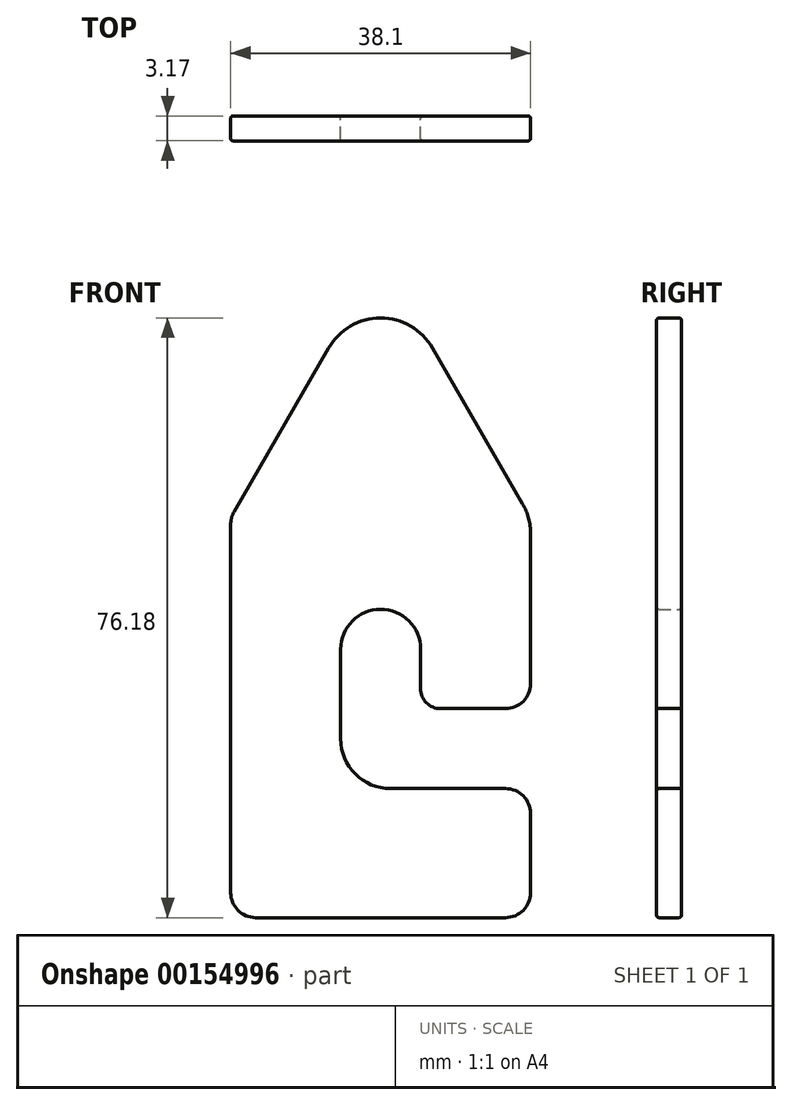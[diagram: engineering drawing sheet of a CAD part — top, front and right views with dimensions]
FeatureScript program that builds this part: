
annotation { "Feature Type Name" : "Feature", "Feature Type Description" : "" }
export const myFeature = defineFeature(function(context is Context, id is Id, definition is map)
    precondition{}
    {
        {
            var Q0;
            Q0=qCreatedBy(makeId("Front.planeOp"),FACE);
            var sketch = newSketch(context, id + "F0", { "sketchPlane" : qUnion([Q0])});
            skLineSegment(sketch, "E0.top", {"start": v(-15.88, -24.24) * mm, "end": v(15.87, -24.24) * mm});
            skLineSegment(sketch, "E0.left", {"start": v(-19.05, 25.7) * mm, "end": v(-19.05, -21.07) * mm});
            skLineSegment(sketch, "E0.right", {"start": v(19.05, 24.52) * mm, "end": v(19.05, 5.48) * mm});
            skLineSegment(sketch, "E1", {"start": v(19.05, -11.03) * mm, "end": v(19.05, -21.07) * mm});
            skLineSegment(sketch, "E2.bottom", {"start": v(15.88, -7.85) * mm, "end": v(1.27, -7.85) * mm});
            skLineSegment(sketch, "E2.top", {"start": v(15.87, 2.3) * mm, "end": v(7.62, 2.3) * mm});
            skLineSegment(sketch, "E2.right", {"start": v(-5.08, -1.5) * mm, "end": v(-5.08, 9.85) * mm});
            skLineSegment(sketch, "E3", {"start": v(-5.08, -7.85) * mm, "end": v(5.08, 2.3) * mm, "construction": true});
            skLineSegment(sketch, "E4", {"start": v(5.08, 4.85) * mm, "end": v(5.08, 9.85) * mm});
            skPoint(sketch, "E5.visualSharp", {"position": v(5.08, 2.3) * mm});
            skArc(sketch, "E5.filletArc", {"start": v(5.08, 4.85) * mm, "mid": v(5.82, 3.05) * mm, "end": v(7.62, 2.3) * mm});
            skPoint(sketch, "E6", {"position": v(0, 9.85) * mm});
            skPoint(sketch, "E7", {"position": v(0, 26.56) * mm});
            skPoint(sketch, "E8.visualSharp", {"position": v(-5.08, -7.85) * mm});
            skArc(sketch, "E8.filletArc", {"start": v(-5.08, -1.5) * mm, "mid": v(-3.22, -6) * mm, "end": v(1.27, -7.85) * mm});
            skPoint(sketch, "E9.visualSharp", {"position": v(-5.08, 9.85) * mm});
            skPoint(sketch, "E10.visualSharp", {"position": v(5.08, 9.85) * mm});
            skPoint(sketch, "E11.visualSharp", {"position": v(19.05, 2.3) * mm});
            skArc(sketch, "E11.filletArc", {"start": v(15.87, 2.3) * mm, "mid": v(18.12, 3.24) * mm, "end": v(19.05, 5.48) * mm});
            skPoint(sketch, "E12.visualSharp", {"position": v(19.05, -7.85) * mm});
            skArc(sketch, "E12.filletArc", {"start": v(19.05, -11.03) * mm, "mid": v(18.12, -8.78) * mm, "end": v(15.88, -7.85) * mm});
            skPoint(sketch, "E13.visualSharp", {"position": v(19.05, -24.24) * mm});
            skArc(sketch, "E13.filletArc", {"start": v(15.87, -24.24) * mm, "mid": v(18.12, -23.31) * mm, "end": v(19.05, -21.07) * mm});
            skPoint(sketch, "E14.visualSharp", {"position": v(-19.05, -24.24) * mm});
            skArc(sketch, "E14.filletArc", {"start": v(-19.05, -21.07) * mm, "mid": v(-18.12, -23.31) * mm, "end": v(-15.88, -24.24) * mm});
            skPoint(sketch, "E15.visualSharp", {"position": v(-19.05, 26.56) * mm});
            skPoint(sketch, "E16.visualSharp", {"position": v(19.05, 26.56) * mm});
            skArc(sketch, "E17", {"start": v(-5.08, 9.85) * mm, "mid": v(0, 14.93) * mm, "end": v(5.08, 9.85) * mm});
            skLineSegment(sketch, "E18", {"start": v(0, 26.56) * mm, "end": v(0, 9.85) * mm, "construction": true});
            skLineSegment(sketch, "E19", {"start": v(-19.05, 26.56) * mm, "end": v(19.05, 26.56) * mm, "construction": true});
            skLineSegment(sketch, "E20", {"start": v(-18.62, 27.3) * mm, "end": v(-6.6, 48.13) * mm});
            skLineSegment(sketch, "E21", {"start": v(18.03, 28.33) * mm, "end": v(6.6, 48.13) * mm});
            skPoint(sketch, "E22.visualSharp", {"position": v(0, 59.56) * mm});
            skArc(sketch, "E22.filletArc", {"start": v(6.6, 48.13) * mm, "mid": v(0, 51.94) * mm, "end": v(-6.6, 48.13) * mm});
            skArc(sketch, "E23.filletArc", {"start": v(19.05, 24.52) * mm, "mid": v(18.8, 26.5) * mm, "end": v(18.03, 28.33) * mm});
            skArc(sketch, "E24.filletArc", {"start": v(-18.62, 27.3) * mm, "mid": v(-18.94, 26.53) * mm, "end": v(-19.05, 25.7) * mm});
            skSolve(sketch);
        }
        {
            var Q0;
            Q0=makeQuery(id+"F0.imprint","IMPRINT",FACE,{"disambiguationData":[TD([[makeQuery(id+"F0.imprint","IMPRINT",EDGE,{"derivedFrom":sQuery(id+"F0.wireOp",EDGE,"E0.top")}),1.0]])]});
            extrude(context, id + "F1", {"entities" : qUnion([Q0]), "depth" : 3.17 * mm});
        }
        {
            var Q0;
            Q0=makeQuery(id+"F1.opExtrude","CAP_FACE",FACE,{"disambiguationData":[OSD([sQuery(id+"F0.wireOp",EDGE,"E0.top"),sQuery(id+"F0.wireOp",EDGE,"E0.left"),sQuery(id+"F0.wireOp",EDGE,"E0.right"),sQuery(id+"F0.wireOp",EDGE,"E1"),sQuery(id+"F0.wireOp",EDGE,"E2.bottom"),sQuery(id+"F0.wireOp",EDGE,"E2.top"),sQuery(id+"F0.wireOp",EDGE,"E2.right"),sQuery(id+"F0.wireOp",EDGE,"E4"),sQuery(id+"F0.wireOp",EDGE,"E5.filletArc"),sQuery(id+"F0.wireOp",EDGE,"E8.filletArc"),sQuery(id+"F0.wireOp",EDGE,"E11.filletArc"),sQuery(id+"F0.wireOp",EDGE,"E12.filletArc"),sQuery(id+"F0.wireOp",EDGE,"E13.filletArc"),sQuery(id+"F0.wireOp",EDGE,"E14.filletArc"),sQuery(id+"F0.wireOp",EDGE,"E17"),sQuery(id+"F0.wireOp",EDGE,"E20"),sQuery(id+"F0.wireOp",EDGE,"E21"),sQuery(id+"F0.wireOp",EDGE,"E22.filletArc"),sQuery(id+"F0.wireOp",EDGE,"E23.filletArc"),sQuery(id+"F0.wireOp",EDGE,"E24.filletArc")])],"isStart":false});
            fillet(context, id + "F2", {"entities" : qUnion([Q0]), "radius" : 0.32 * mm, "tangentPropagation" : true, "allowEdgeOverflow" : false});
        }
        {
            var Q0;
            Q0=makeQuery(id+"F1.opExtrude","CAP_FACE",FACE,{"disambiguationData":[OSD([sQuery(id+"F0.wireOp",EDGE,"E0.top"),sQuery(id+"F0.wireOp",EDGE,"E0.left"),sQuery(id+"F0.wireOp",EDGE,"E0.right"),sQuery(id+"F0.wireOp",EDGE,"E1"),sQuery(id+"F0.wireOp",EDGE,"E2.bottom"),sQuery(id+"F0.wireOp",EDGE,"E2.top"),sQuery(id+"F0.wireOp",EDGE,"E2.right"),sQuery(id+"F0.wireOp",EDGE,"E4"),sQuery(id+"F0.wireOp",EDGE,"E5.filletArc"),sQuery(id+"F0.wireOp",EDGE,"E8.filletArc"),sQuery(id+"F0.wireOp",EDGE,"E11.filletArc"),sQuery(id+"F0.wireOp",EDGE,"E12.filletArc"),sQuery(id+"F0.wireOp",EDGE,"E13.filletArc"),sQuery(id+"F0.wireOp",EDGE,"E14.filletArc"),sQuery(id+"F0.wireOp",EDGE,"E17"),sQuery(id+"F0.wireOp",EDGE,"E20"),sQuery(id+"F0.wireOp",EDGE,"E21"),sQuery(id+"F0.wireOp",EDGE,"E22.filletArc"),sQuery(id+"F0.wireOp",EDGE,"E23.filletArc"),sQuery(id+"F0.wireOp",EDGE,"E24.filletArc")])],"isStart":true});
            fillet(context, id + "F3", {"entities" : qUnion([Q0]), "radius" : 0.32 * mm, "tangentPropagation" : true, "allowEdgeOverflow" : false});
        }
    });
